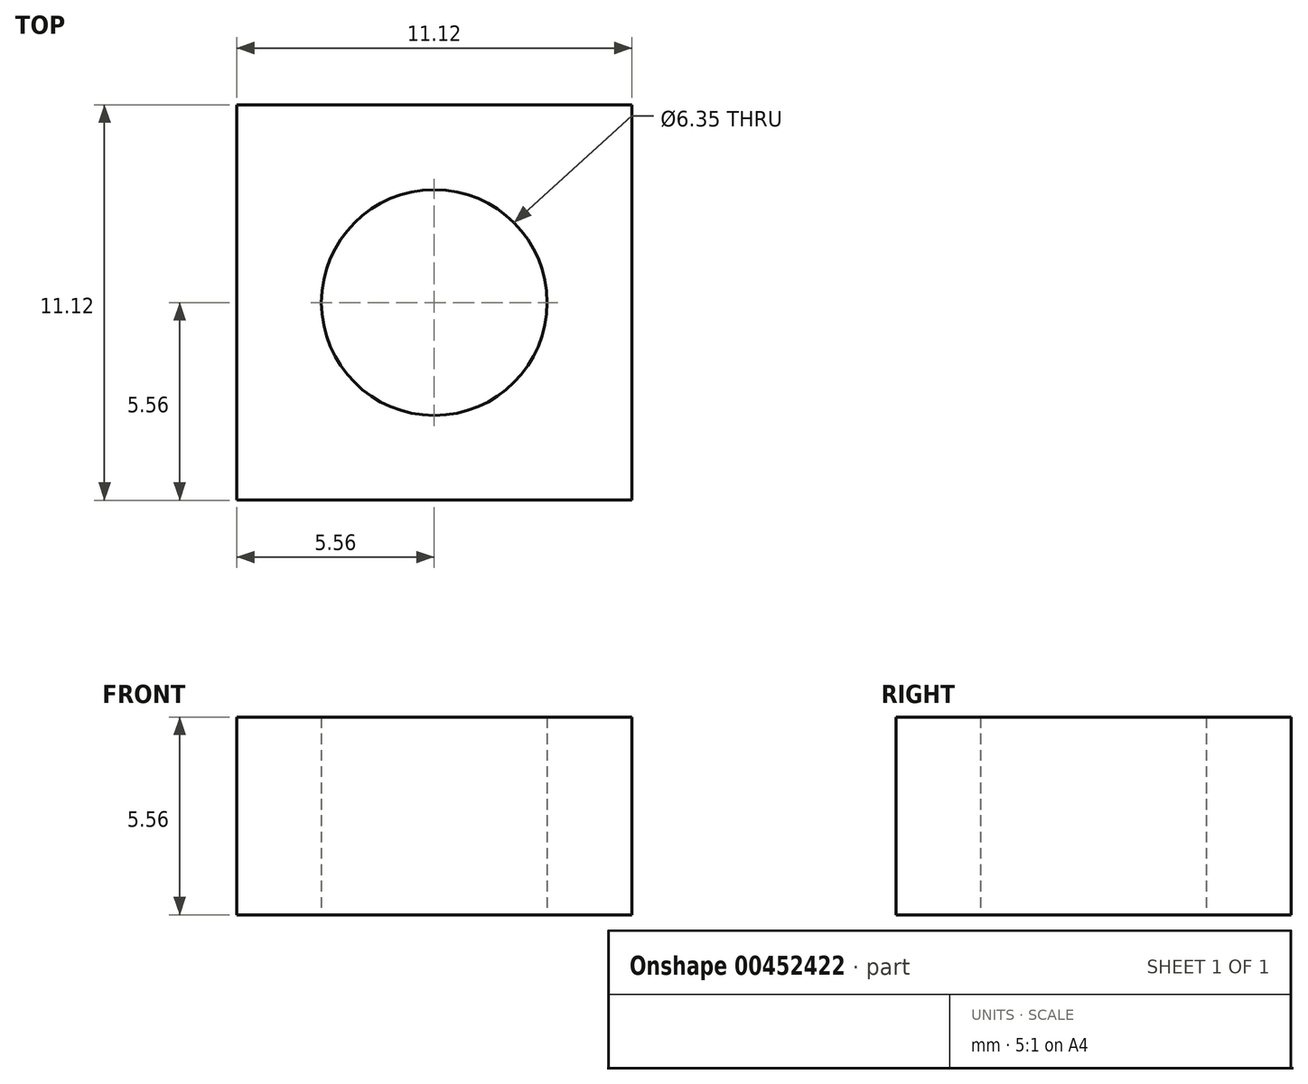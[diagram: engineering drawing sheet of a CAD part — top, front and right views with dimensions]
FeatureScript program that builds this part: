
annotation { "Feature Type Name" : "Feature", "Feature Type Description" : "" }
export const myFeature = defineFeature(function(context is Context, id is Id, definition is map)
    precondition{}
    {
        {
            var Q0;
            Q0=qCreatedBy(makeId("Top.planeOp"),FACE);
            var sketch = newSketch(context, id + "F0", { "sketchPlane" : qUnion([Q0])});
            skLineSegment(sketch, "E0.bottom", {"start": v(5.56, -5.56) * mm, "end": v(-5.56, -5.56) * mm});
            skLineSegment(sketch, "E0.top", {"start": v(5.56, 5.56) * mm, "end": v(-5.56, 5.56) * mm});
            skLineSegment(sketch, "E0.left", {"start": v(5.56, -5.56) * mm, "end": v(5.56, 5.56) * mm});
            skLineSegment(sketch, "E0.right", {"start": v(-5.56, -5.56) * mm, "end": v(-5.56, 5.56) * mm});
            skPoint(sketch, "E0.middle", {"position": v(0, 0) * mm});
            skCircle(sketch, "E1", {"center": v(0, 0) * mm, "radius": 3.18 * mm});
            skSolve(sketch);
        }
        {
            var Q0;
            Q0=makeQuery(id+"F0.imprint","IMPRINT",FACE,{"disambiguationData":[TD([[makeQuery(id+"F0.imprint","IMPRINT",EDGE,{"derivedFrom":sQuery(id+"F0.wireOp",EDGE,"E0.bottom")}),-1.0]])]});
            extrude(context, id + "F1", {"entities" : qUnion([Q0]), "depth" : 5.56 * mm});
        }
    });
